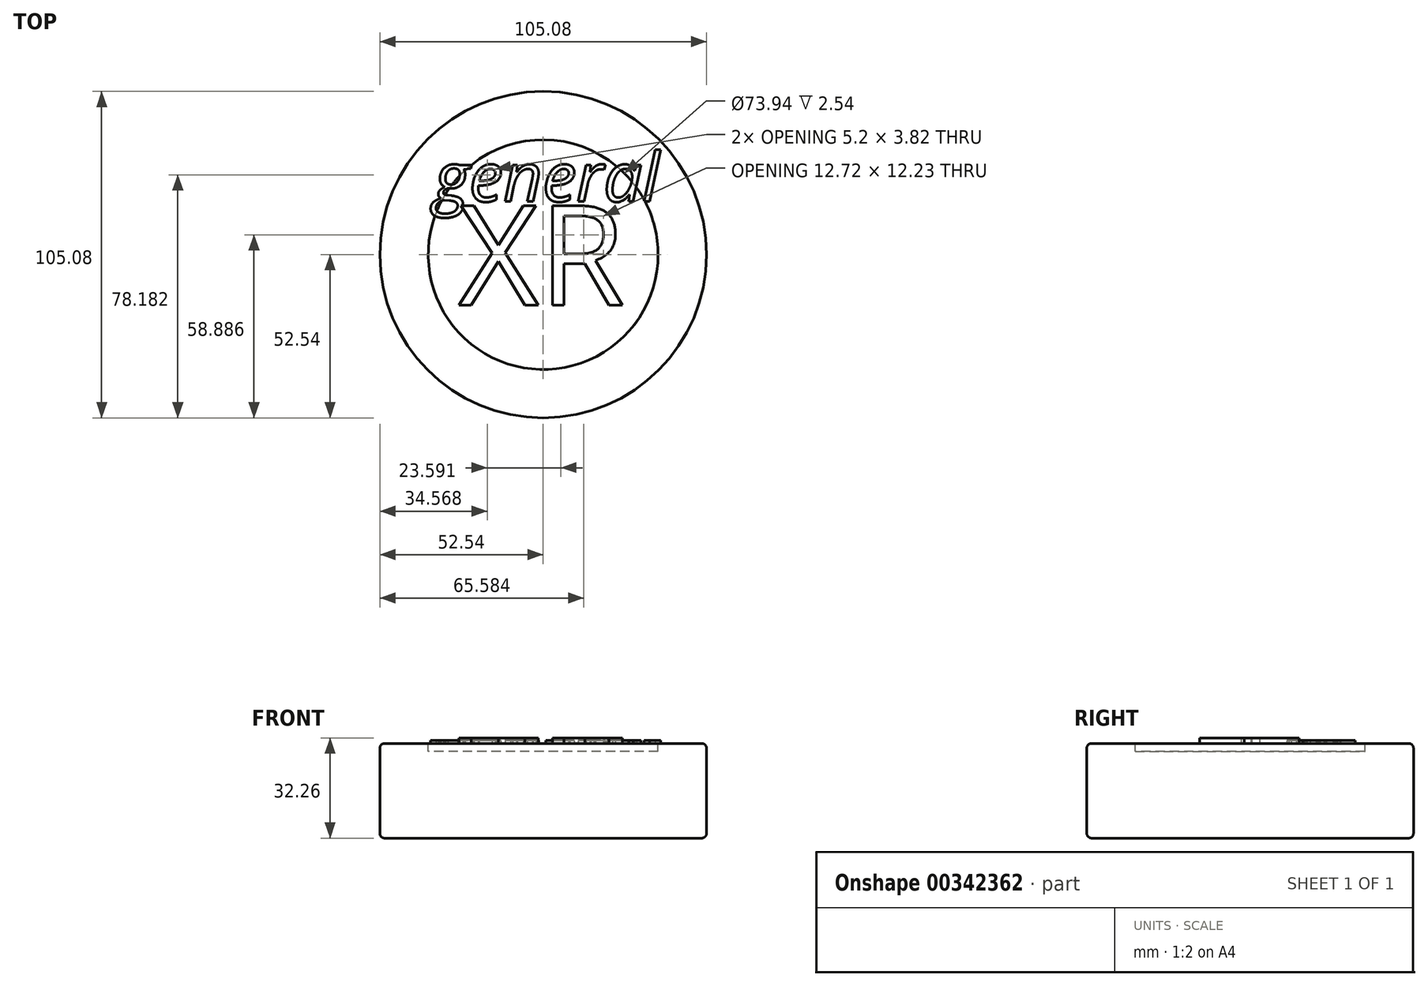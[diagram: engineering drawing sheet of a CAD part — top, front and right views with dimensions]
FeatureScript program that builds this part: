
annotation { "Feature Type Name" : "Feature", "Feature Type Description" : "" }
export const myFeature = defineFeature(function(context is Context, id is Id, definition is map)
    precondition{}
    {
        {
            var Q0;
            Q0=qCreatedBy(makeId("Top.planeOp"),FACE);
            var sketch = newSketch(context, id + "F0", { "sketchPlane" : qUnion([Q0])});
            skCircle(sketch, "E0", {"center": v(0, 0) * mm, "radius": 52.54 * mm});
            skSolve(sketch);
        }
        {
            var Q0;
            Q0=makeQuery(id+"F0.imprint","IMPRINT",FACE,{"disambiguationData":[TD([[makeQuery(id+"F0.imprint","IMPRINT",EDGE,{"derivedFrom":sQuery(id+"F0.wireOp",EDGE,"E0")}),1.0]])]});
            extrude(context, id + "F1", {"entities" : qUnion([Q0]), "depth" : 30.48 * mm});
        }
        {
            var Q0;
            Q0=makeQuery(id+"F1.opExtrude","CAP_EDGE",EDGE,{"disambiguationData":[OSD([sQuery(id+"F0.wireOp",EDGE,"E0")])],"isStart":false});
            var Q1;
            Q1=makeQuery(id+"F1.opExtrude","CAP_EDGE",EDGE,{"disambiguationData":[OSD([sQuery(id+"F0.wireOp",EDGE,"E0")])],"isStart":true});
            fillet(context, id + "F2", {"entities" : qUnion([Q0, Q1]), "radius" : 1.52 * mm, "tangentPropagation" : true, "allowEdgeOverflow" : false});
        }
        {
            var Q0;
            Q0=makeQuery(id+"F1.opExtrude","CAP_FACE",FACE,{"disambiguationData":[OSD([sQuery(id+"F0.wireOp",EDGE,"E0")])],"isStart":false});
            var sketch = newSketch(context, id + "F3", { "sketchPlane" : qUnion([Q0])});
            skCircle(sketch, "E1", {"center": v(0, 0) * mm, "radius": 36.97 * mm});
            skSolve(sketch);
        }
        {
            var Q0;
            Q0=makeQuery(id+"F3.imprint","IMPRINT",FACE,{"disambiguationData":[TD([[makeQuery(id+"F3.imprint","IMPRINT",EDGE,{"derivedFrom":sQuery(id+"F3.wireOp",EDGE,"E1")}),-1.0]])]});
            var sketch = newSketch(context, id + "F4", { "sketchPlane" : qUnion([Q0])});
            skText(sketch, "E2", { "text": "XR\n", "fontName": "OpenSans-Regular.ttf"});
            const initialGuessF4  = {"E2": [-0.0273, -0.01627, 1, 0, 0.03227]};
            skSetInitialGuess(sketch, initialGuessF4);
            skSolve(sketch);
        }
        {
            var Q0;
            Q0 = qSketchRegion(id + "F4", true);
            extrude(context, id + "F5", {"entities" : qUnion([Q0]), "operationType" : NewBodyOperationType.ADD, "depth" : 1.78 * mm});
        }
        {
            var Q0;
            Q0=makeQuery(id+"F3.imprint","IMPRINT",FACE,{"disambiguationData":[TD([[makeQuery(id+"F3.imprint","IMPRINT",EDGE,{"derivedFrom":sQuery(id+"F3.wireOp",EDGE,"E1")}),-1.0]])]});
            var sketch = newSketch(context, id + "F6", { "sketchPlane" : qUnion([Q0])});
            skText(sketch, "E3", { "text": "general", "fontName": "OpenSans-Italic.ttf"});
            const initialGuessF6  = {"E3": [-0.03483, 0.01708, 1, 0, 0.01587]};
            skSetInitialGuess(sketch, initialGuessF6);
            skSolve(sketch);
        }
        {
            var Q0;
            Q0 = qSketchRegion(id + "F6", true);
            extrude(context, id + "F7", {"entities" : qUnion([Q0]), "operationType" : NewBodyOperationType.ADD, "depth" : 1.02 * mm});
        }
        {
            var Q0;
            Q0=makeQuery(id+"F3.imprint","IMPRINT",FACE,{"disambiguationData":[TD([[makeQuery(id+"F3.imprint","IMPRINT",EDGE,{"derivedFrom":sQuery(id+"F3.wireOp",EDGE,"E1")}),1.0]])]});
            extrude(context, id + "F8", {"entities" : qUnion([Q0]), "operationType" : NewBodyOperationType.REMOVE, "oppositeDirection" : true, "depth" : 0.76 * mm});
        }
        {
            var Q0;
            Q0=makeQuery(id+"F8.boolean.opBoolean","COPY",FACE,{"derivedFrom":makeQuery(id+"F8.opExtrude","CAP_FACE",FACE,{"disambiguationData":[OSD([sQuery(id+"F3.wireOp",EDGE,"E1")])],"isStart":false})});
            extrude(context, id + "F9", {"entities" : qUnion([Q0]), "operationType" : NewBodyOperationType.REMOVE, "oppositeDirection" : true, "depth" : 1.78 * mm});
        }
    });
